# Revit family: QF_Vollrath_69505
name_source: partatom
category: Specialty Equipment
revit_build: Autodesk Revit 2016 (Build: 20151007_0715(x64)
units: mm (PartAtom-declared; Revit-internal decimal feet)

## family parameters
Always vertical = Yes
Cut with Voids When Loaded = No
OmniClass Number = 23.40.40.14.17.14
OmniClass Title = Hot Plates
Part Type = Normal
Room Calculation Point = No
Round Connector Dimension = Use Diameter
Shared = No
Work Plane-Based = No

## types (2) — shared parameters
Assembly Code = E1090320
CSI MasterFormat = 11 44 00
Conn Plug = NEMA 6-20P
Cycle = 60 Hz
Description = Induction Range, Drop-In
FL Amps = 15 A
Manufacturer = Vollrath
Model = 69505
Number of Poles = 1
Phase = 1
URL = www.vollrathco.com
Weight in Pounds = 27

## per-type parameters (varying)
| type | Apparent Power | Volts | Watts |
| 208V | 3037 VA | 208 V | 3000 W |
| 240V | 3504 VA | 240 V | 3500 W |

## geometry (parser evidence)
native form markers: Blend x6, Sweep x3
no freeform markers — native parametric forms only
